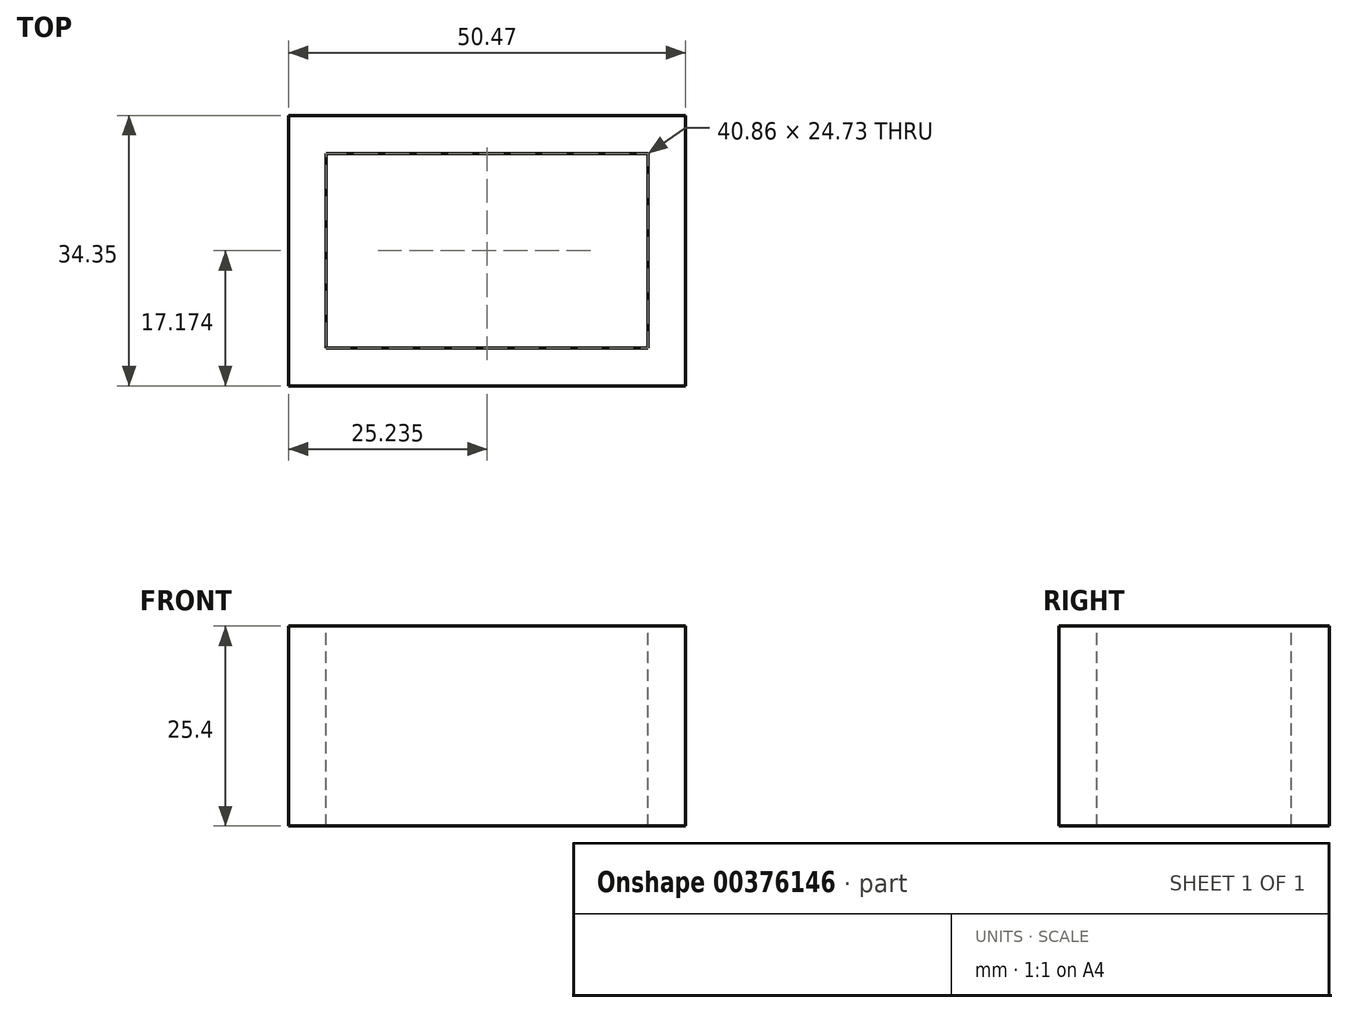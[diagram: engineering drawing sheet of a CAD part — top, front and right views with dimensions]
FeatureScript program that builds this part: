
annotation { "Feature Type Name" : "Feature", "Feature Type Description" : "" }
export const myFeature = defineFeature(function(context is Context, id is Id, definition is map)
    precondition{}
    {
        {
            var Q0;
            Q0=qCreatedBy(makeId("Top.planeOp"),FACE);
            var sketch = newSketch(context, id + "F0", { "sketchPlane" : qUnion([Q0])});
            skLineSegment(sketch, "E0.bottom", {"start": v(0, 0) * mm, "end": v(50.47, 0) * mm});
            skLineSegment(sketch, "E0.top", {"start": v(0, 34.35) * mm, "end": v(50.47, 34.35) * mm});
            skLineSegment(sketch, "E0.left", {"start": v(0, 0) * mm, "end": v(0, 34.35) * mm});
            skLineSegment(sketch, "E0.right", {"start": v(50.47, 0) * mm, "end": v(50.47, 34.35) * mm});
            skSolve(sketch);
        }
        {
            var Q0;
            Q0 = qSketchRegion(id + "F0", true);
            extrude(context, id + "F1", {"entities" : qUnion([Q0]), "depth" : 25.4 * mm});
        }
        {
            var Q0;
            Q0=makeQuery(id+"F1.opExtrude","CAP_FACE",FACE,{"disambiguationData":[OSD([sQuery(id+"F0.wireOp",EDGE,"E0.bottom"),sQuery(id+"F0.wireOp",EDGE,"E0.top"),sQuery(id+"F0.wireOp",EDGE,"E0.left"),sQuery(id+"F0.wireOp",EDGE,"E0.right")])],"isStart":false});
            var sketch = newSketch(context, id + "F2", { "sketchPlane" : qUnion([Q0])});
            skLineSegment(sketch, "E1", {"start": v(0, 29.54) * mm, "end": v(4.8, 29.54) * mm, "construction": true});
            skLineSegment(sketch, "E2", {"start": v(4.8, 29.54) * mm, "end": v(4.8, 34.35) * mm, "construction": true});
            skLineSegment(sketch, "E3.bottom", {"start": v(4.8, 29.54) * mm, "end": v(45.66, 29.54) * mm});
            skLineSegment(sketch, "E3.top", {"start": v(4.8, 4.8) * mm, "end": v(45.66, 4.8) * mm});
            skLineSegment(sketch, "E3.left", {"start": v(4.8, 29.54) * mm, "end": v(4.8, 4.8) * mm});
            skLineSegment(sketch, "E3.right", {"start": v(45.66, 29.54) * mm, "end": v(45.66, 4.8) * mm});
            skLineSegment(sketch, "E4", {"start": v(45.66, 4.8) * mm, "end": v(45.66, 0) * mm, "construction": true});
            skLineSegment(sketch, "E5", {"start": v(45.66, 4.8) * mm, "end": v(50.47, 4.8) * mm, "construction": true});
            skSolve(sketch);
        }
        {
            var Q0;
            Q0 = qSketchRegion(id + "F2", true);
            extrude(context, id + "F3", {"entities" : qUnion([Q0]), "operationType" : NewBodyOperationType.REMOVE, "oppositeDirection" : true, "depth" : 25.4 * mm});
        }
    });
